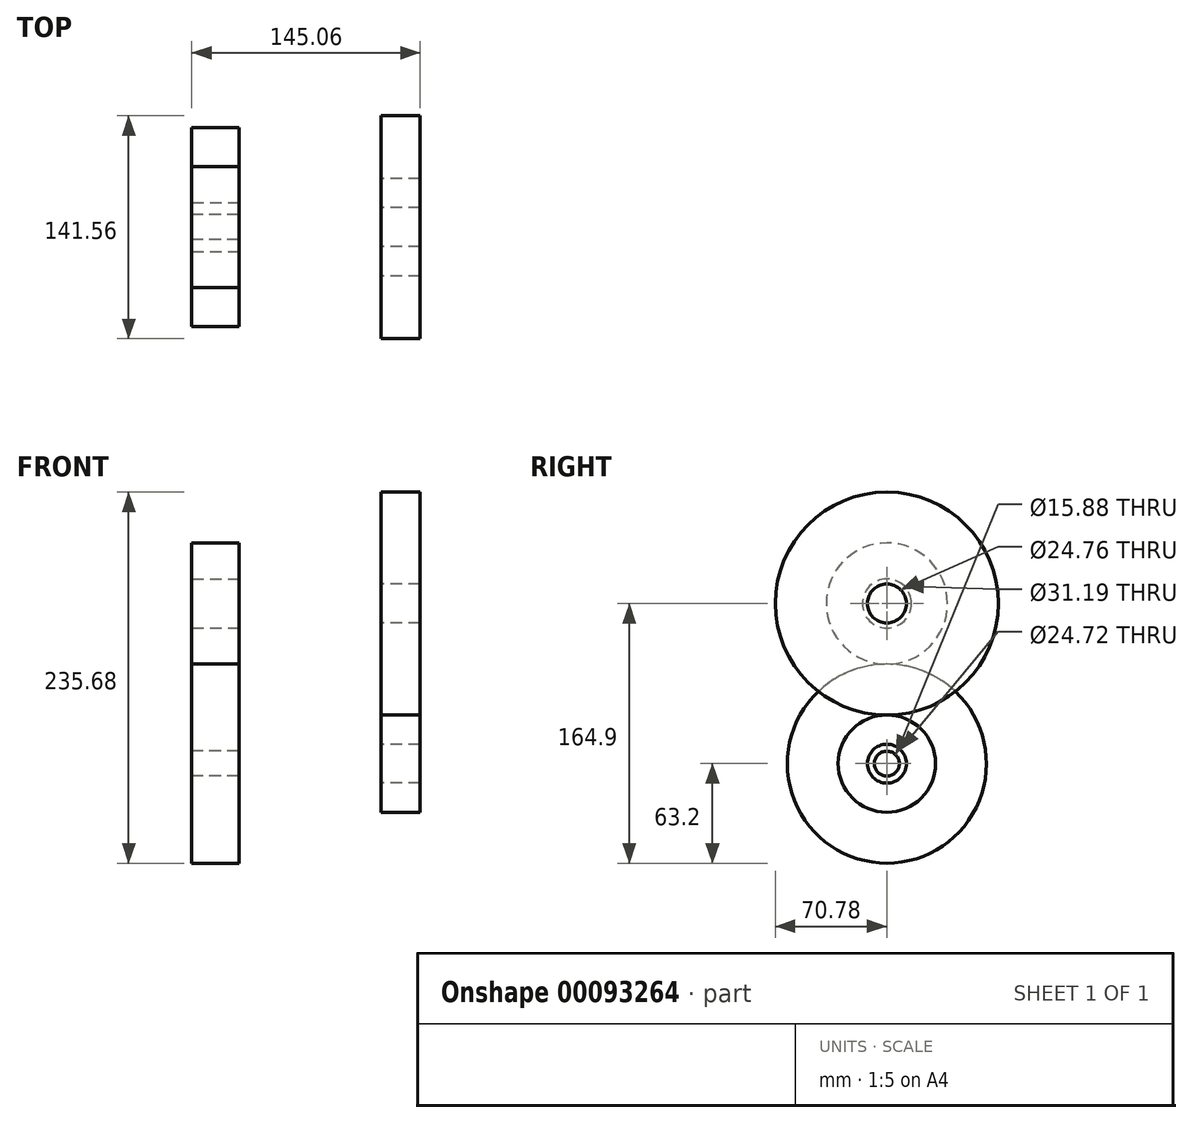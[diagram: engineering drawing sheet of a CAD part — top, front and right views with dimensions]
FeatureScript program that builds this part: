
annotation { "Feature Type Name" : "Feature", "Feature Type Description" : "" }
export const myFeature = defineFeature(function(context is Context, id is Id, definition is map)
    precondition{}
    {
        {
            var Q0;
            Q0=qCreatedBy(makeId("Front.planeOp"),FACE);
            var sketch = newSketch(context, id + "F0", { "sketchPlane" : qUnion([Q0])});
            skLineSegment(sketch, "E0.bottom", {"start": v(58.78, 50.85) * mm, "end": v(-58.78, 50.85) * mm});
            skLineSegment(sketch, "E0.top", {"start": v(58.78, -50.85) * mm, "end": v(-58.78, -50.85) * mm});
            skLineSegment(sketch, "E0.left", {"start": v(58.78, 50.85) * mm, "end": v(58.78, -50.85) * mm});
            skLineSegment(sketch, "E0.right", {"start": v(-58.78, 50.85) * mm, "end": v(-58.78, -50.85) * mm});
            skPoint(sketch, "E0.middle", {"position": v(0, 0) * mm});
            skSolve(sketch);
        }
        {
            var Q0;
            Q0=qCreatedBy(makeId("Right.planeOp"),FACE);
            var Q1;
            Q1=sQuery(id+"F0.wireOp",VERTEX,"E0.right.start");
            cPlane(context, id + "F1", {"entities" : qUnion([Q0, Q1]), "cplaneType" : CPlaneType.PLANE_POINT, "offset" : 50 * mm, "oppositeDirection" : true, "width" : 152.4 * mm, "height" : 152.4 * mm});
        }
        {
            var Q0;
            Q0=qCreatedBy(id+"F1.planeOp",FACE);
            var sketch = newSketch(context, id + "F2", { "sketchPlane" : qUnion([Q0])});
            skCircle(sketch, "E1", {"center": v(0, 50.85) * mm, "radius": 38.5 * mm});
            skCircle(sketch, "E2", {"center": v(0, -50.85) * mm, "radius": 63.2 * mm});
            skCircle(sketch, "E3", {"center": v(0, -50.85) * mm, "radius": 7.94 * mm});
            skCircle(sketch, "E4", {"center": v(0, 50.85) * mm, "radius": 15.6 * mm});
            skSolve(sketch);
        }
        {
            var Q0;
            Q0=qCreatedBy(makeId("Right.planeOp"),FACE);
            var Q1;
            Q1=sQuery(id+"F0.wireOp",VERTEX,"E0.left.end");
            cPlane(context, id + "F3", {"entities" : qUnion([Q0, Q1]), "cplaneType" : CPlaneType.PLANE_POINT, "offset" : 150 * mm, "width" : 150 * mm, "height" : 150 * mm});
        }
        {
            var Q0;
            Q0=qCreatedBy(id+"F3.planeOp",FACE);
            var sketch = newSketch(context, id + "F4", { "sketchPlane" : qUnion([Q0])});
            skCircle(sketch, "E5", {"center": v(0, -50.85) * mm, "radius": 12.36 * mm});
            skCircle(sketch, "E6", {"center": v(0, 50.85) * mm, "radius": 12.38 * mm});
            skCircle(sketch, "E7", {"center": v(0, 50.85) * mm, "radius": 70.78 * mm});
            skCircle(sketch, "E8", {"center": v(0, -50.85) * mm, "radius": 30.92 * mm});
            skSolve(sketch);
        }
        {
            var Q0;
            Q0=makeQuery(id+"F2.imprint","IMPRINT",FACE,{"disambiguationData":[TD([[makeQuery(id+"F2.imprint","IMPRINT",EDGE,{"derivedFrom":sQuery(id+"F2.wireOp",EDGE,"E2")}),1.0]])]});
            extrude(context, id + "F5", {"entities" : qUnion([Q0]), "endBound" : BoundingType.SYMMETRIC, "depth" : 30 * mm});
        }
        {
            var Q0;
            Q0=makeQuery(id+"F2.imprint","IMPRINT",FACE,{"disambiguationData":[TD([[makeQuery(id+"F2.imprint","IMPRINT",EDGE,{"derivedFrom":sQuery(id+"F2.wireOp",EDGE,"E1")}),1.0]])]});
            var Q1;
            Q1=makeQuery(id+"F5.opExtrude","CAP_FACE",FACE,{"disambiguationData":[OSD([sQuery(id+"F2.wireOp",EDGE,"E2")])],"isStart":true});
            var Q2;
            Q2=makeQuery(id+"F5.opExtrude","CAP_FACE",FACE,{"disambiguationData":[OSD([sQuery(id+"F2.wireOp",EDGE,"E2")])],"isStart":false});
            extrude(context, id + "F6", {"entities" : qUnion([Q0]), "endBound" : BoundingType.UP_TO_SURFACE, "oppositeDirection" : true, "endBoundEntityFace" : qUnion([Q1]), "depth" : 64.35 * mm, "hasSecondDirection" : true, "secondDirectionBound" : SecondDirectionBoundingType.UP_TO_SURFACE, "secondDirectionOppositeDirection" : false, "secondDirectionBoundEntityFace" : qUnion([Q2]), "secondDirectionDepth" : 25.4 * mm});
        }
        {
            var Q0;
            Q0=makeQuery(id+"F4.imprint","IMPRINT",FACE,{"disambiguationData":[TD([[makeQuery(id+"F4.imprint","IMPRINT",EDGE,{"derivedFrom":sQuery(id+"F4.wireOp",EDGE,"E5")}),-1.0]])]});
            extrude(context, id + "F7", {"entities" : qUnion([Q0]), "endBound" : BoundingType.SYMMETRIC, "depth" : 25 * mm});
        }
        {
            var Q0;
            Q0=makeQuery(id+"F4.imprint","IMPRINT",FACE,{"disambiguationData":[TD([[makeQuery(id+"F4.imprint","IMPRINT",EDGE,{"derivedFrom":sQuery(id+"F4.wireOp",EDGE,"E6")}),-1.0]])]});
            extrude(context, id + "F8", {"entities" : qUnion([Q0]), "operationType" : NewBodyOperationType.ADD, "endBound" : BoundingType.SYMMETRIC, "depth" : 25 * mm});
        }
    });
